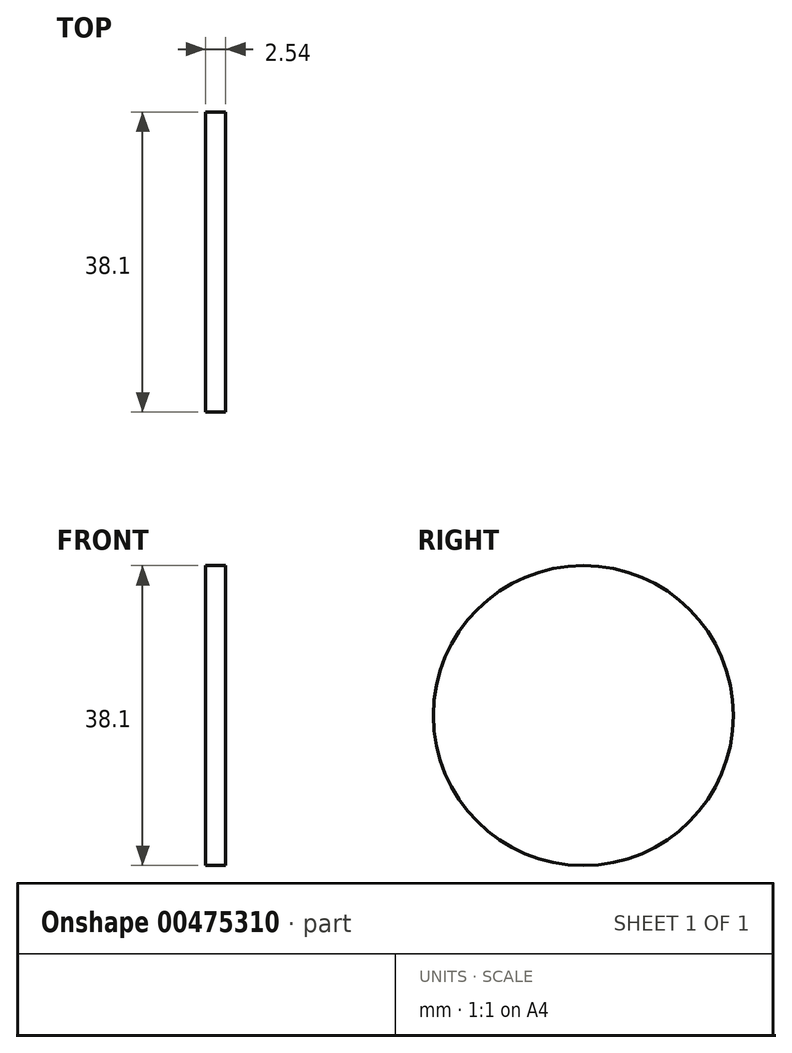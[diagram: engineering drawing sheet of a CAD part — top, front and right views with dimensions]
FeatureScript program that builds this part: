
annotation { "Feature Type Name" : "Feature", "Feature Type Description" : "" }
export const myFeature = defineFeature(function(context is Context, id is Id, definition is map)
    precondition{}
    {
        {
            var Q0;
            Q0=qCreatedBy(makeId("Right.planeOp"),FACE);
            var sketch = newSketch(context, id + "F0", { "sketchPlane" : qUnion([Q0])});
            skCircle(sketch, "E0", {"center": v(-38.27, 52.44) * mm, "radius": 19.05 * mm});
            skSolve(sketch);
        }
        {
            var Q0;
            Q0=makeQuery(id+"F0.imprint","IMPRINT",FACE,{"disambiguationData":[TD([[makeQuery(id+"F0.imprint","IMPRINT",EDGE,{"derivedFrom":sQuery(id+"F0.wireOp",EDGE,"E0")}),1.0]])]});
            extrude(context, id + "F1", {"entities" : qUnion([Q0]), "depth" : 2.54 * mm});
        }
    });
